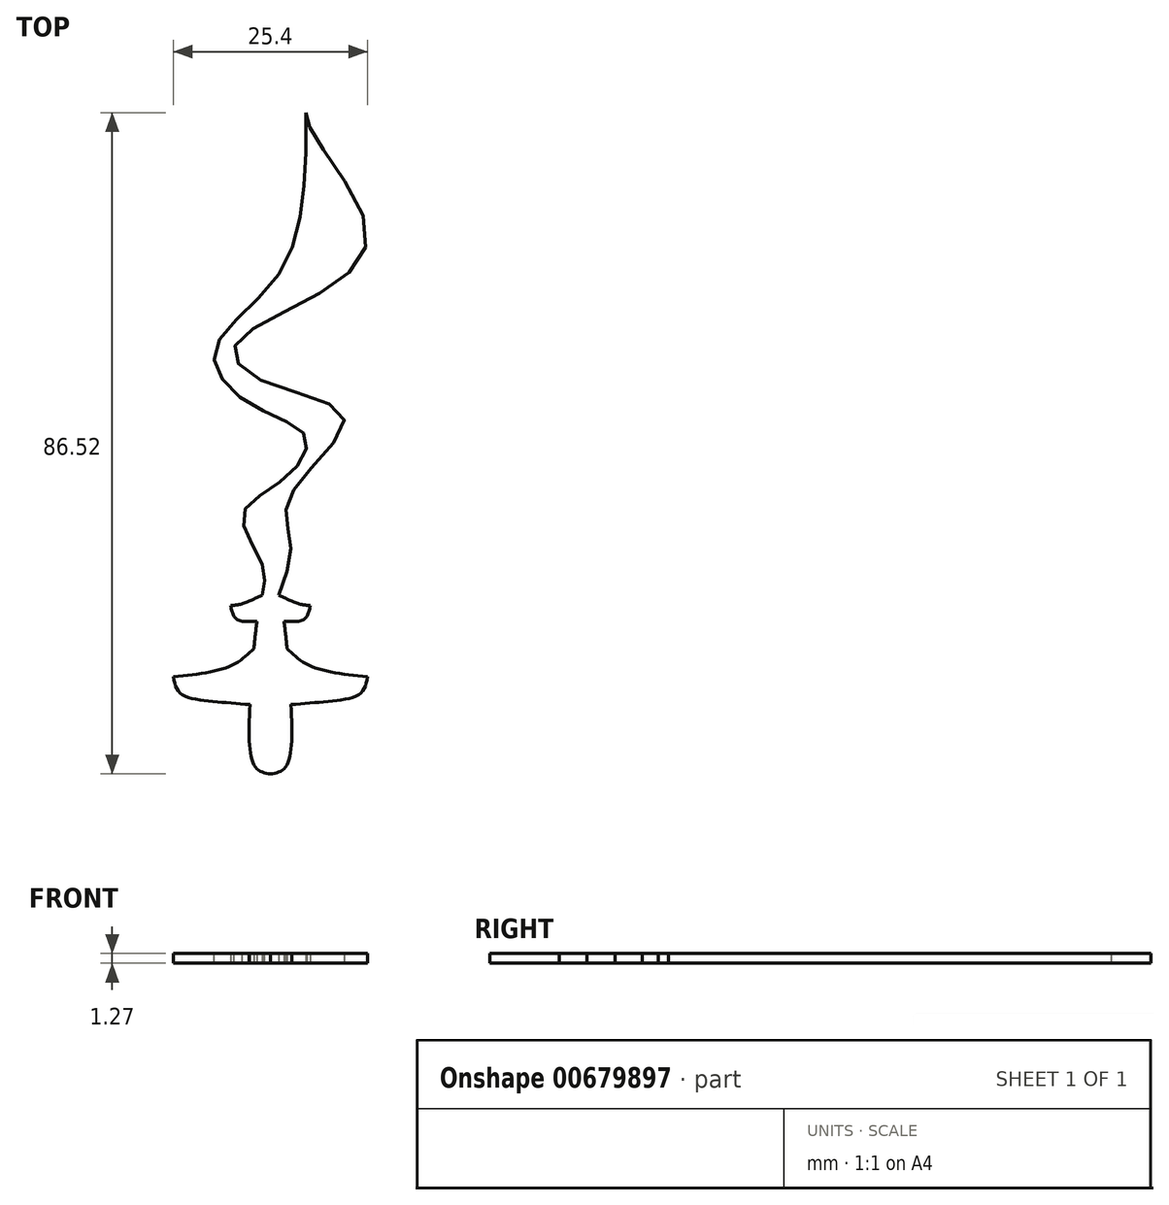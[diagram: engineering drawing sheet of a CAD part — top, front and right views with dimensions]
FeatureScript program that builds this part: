
annotation { "Feature Type Name" : "Feature", "Feature Type Description" : "" }
export const myFeature = defineFeature(function(context is Context, id is Id, definition is map)
    precondition{}
    {
        {
            var Q0;
            Q0=qCreatedBy(makeId("Top.planeOp"),FACE);
            var sketch = newSketch(context, id + "F0", { "sketchPlane" : qUnion([Q0])});
            skCircle(sketch, "E0", {"center": v(0, 0) * mm, "radius": 12.7 * mm, "construction": true});
            skFitSpline(sketch, "E1", {"points": [v(0, 12.7) * mm, v(-1.08, 10.68) * mm, v(-2.6, -2.1) * mm, v(-2, -11.78) * mm, v(0, -12.7) * mm], "startDerivative": vector(-7.31, -9.53) * mm, "endDerivative": vector(14.87, -2.3) * mm});
            skFitSpline(sketch, "E2", {"points": [v(-2.69, -3.62) * mm, v(-8.4, -3.11) * mm, v(-11.85, -2.1) * mm, v(-12.7, 0) * mm], "startDerivative": vector(-14.2, 1.1) * mm, "endDerivative": vector(-1.73, 9.18) * mm});
            skFitSpline(sketch, "E3", {"points": [v(-2.16, 3.7) * mm, v(-5.2, 1.43) * mm, v(-12.7, 0) * mm], "startDerivative": vector(-6.24, -6.14) * mm, "endDerivative": vector(-14.38, -1.54) * mm});
            skFitSpline(sketch, "E4", {"points": [v(-1.08, 10.68) * mm, v(-3.94, 9.5) * mm, v(-5.2, 9.34) * mm], "startDerivative": vector(-5.14, -2.4) * mm, "endDerivative": vector(-2.94, -0.14) * mm});
            skFitSpline(sketch, "E5", {"points": [v(-1.76, 7.28) * mm, v(-4.45, 7.57) * mm, v(-5.2, 9.34) * mm], "startDerivative": vector(-5.84, -0.37) * mm, "endDerivative": vector(-0.9, 4.62) * mm});
            skFitSpline(sketch, "E6.MirrorCS", {"points": [v(0, 12.7) * mm, v(1.08, 10.68) * mm, v(2.6, -2.1) * mm, v(2, -11.78) * mm, v(0, -12.7) * mm], "startDerivative": vector(7.31, -9.53) * mm, "endDerivative": vector(-14.87, -2.3) * mm});
            skFitSpline(sketch, "E7.MirrorCS", {"points": [v(1.76, 7.28) * mm, v(4.45, 7.57) * mm, v(5.2, 9.34) * mm], "startDerivative": vector(5.84, -0.37) * mm, "endDerivative": vector(0.9, 4.62) * mm});
            skFitSpline(sketch, "E8.MirrorCS", {"points": [v(1.08, 10.68) * mm, v(3.94, 9.5) * mm, v(5.2, 9.34) * mm], "startDerivative": vector(5.14, -2.4) * mm, "endDerivative": vector(2.94, -0.14) * mm});
            skFitSpline(sketch, "E9.MirrorCS", {"points": [v(2.16, 3.7) * mm, v(5.2, 1.43) * mm, v(12.7, 0) * mm], "startDerivative": vector(6.24, -6.14) * mm, "endDerivative": vector(14.38, -1.54) * mm});
            skFitSpline(sketch, "E10.MirrorCS", {"points": [v(2.69, -3.62) * mm, v(8.4, -3.11) * mm, v(11.85, -2.1) * mm, v(12.7, 0) * mm], "startDerivative": vector(14.2, 1.1) * mm, "endDerivative": vector(1.73, 9.18) * mm});
            skFitSpline(sketch, "E11", {"points": [v(-1.08, 10.68) * mm, v(-1.08, 14.74) * mm, v(-3.64, 21.13) * mm, v(1.83, 25.96) * mm, v(4.64, 31.31) * mm, v(-2.89, 35.86) * mm, v(-7.29, 42.63) * mm, v(1.08, 52.67) * mm, v(4.64, 68.6) * mm], "startDerivative": vector(9.64, 43.33) * mm, "endDerivative": vector(4.45, 99.19) * mm});
            skFitSpline(sketch, "E12", {"points": [v(1.08, 10.68) * mm, v(2.69, 16.93) * mm, v(2, 21.35) * mm, v(4.64, 26.57) * mm, v(9.58, 34.07) * mm, v(-1.08, 38.75) * mm, v(-4.74, 43.03) * mm, v(4.64, 49.2) * mm, v(12.66, 57.76) * mm, v(5.83, 70.6) * mm, v(4.64, 73.82) * mm], "startDerivative": vector(27.64, 72.47) * mm, "endDerivative": vector(-7, 39.8) * mm});
            skFitSpline(sketch, "E13", {"points": [v(4.64, 68.6) * mm, v(4.64, 73.82) * mm], "startDerivative": vector(0, 5.22) * mm, "endDerivative": vector(0, 5.22) * mm});
            skSolve(sketch);
        }
        {
            var Q0;
            Q0 = qSketchRegion(id + "F0", true);
            extrude(context, id + "F1", {"entities" : qUnion([Q0]), "depth" : 1.27 * mm, "offsetDistance" : 25.4 * mm});
        }
    });
